# Revit family: Liv_In-Wall_Water Dispenser-Elkay-LBWDC00BKC
name_source: partatom
category: Plumbing Fixtures
units: mm (PartAtom-declared; Revit-internal decimal feet)

## family parameters
Cut with Voids When Loaded = No
Host = Face
Maintain Annotation Orientation = No
OmniClass Number = 23.65.70.14.11
OmniClass Title = Drinking Fountains/Coolers
Part Type = Normal
Room Calculation Point = No
Round Connector Dimension = Use Diameter
Shared = No

## types (1)
- LBWDC00BKC (Commercial Filtered Water Dispenser Non refrigerated Midnight)
    Activation Method = Electronic Bottle Filler Sensor
    Approx. Shipping Weight (lbs) = 41
    Assembly Code = D2010
    CW Connection = No
    Current = 0 A
    Default Elevation = 48 "
    Description = Liv®  In-Wall Filtered Water Dispenser Non-refrigerated Midnight
    Height = 28 "
    Inlet connection = 0.38 "
    Length = 5.13 "
    Main Material = Finish-Elkay-Stainless Steel
    Manufacturer = Elkay Manufacturer Company
    Manufacturer Brand = Elkay (by Zurn Elkay Water Solutions)
    Material_Front Panel = Finish-Elkay-Midnight Black
    Model = LBWDC00BKC
    Number of Poles = 1
    Outlet connection = 1.25 "
    Power Factor = 0
    Product Documentation Link = https://www.elkayfiles.com
    Product Installation Sheet URL = https://www.elkayfiles.com
    Product Page URL = https://www.elkay.com
    Product Weight (lbs) = 25
    Product data URL = https://www.bimobject.com
    Repair Parts URL = https://www.elkayfiles.com
    Second material = Elkay-Transparent
    URL = https://www.elkay.com
    Voltage = 115 V
    Waste Connection = No
    Width = 18 "

## geometry (parser evidence)
native form markers: Sweep x5
no freeform markers — native parametric forms only
